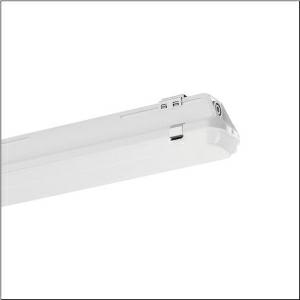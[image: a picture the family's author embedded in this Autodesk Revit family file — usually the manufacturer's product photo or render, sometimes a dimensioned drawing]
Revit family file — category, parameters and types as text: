
# Revit family: monsun_r__12_51fp12mp4b0q_0d1b
name_source: partatom
category: Lighting Fixtures
units: mm (PartAtom-declared; Revit-internal decimal feet)

## family parameters
Cut with Voids When Loaded = No
Host = Face
Light Source = No
Part Type = Normal
Room Calculation Point = No
Round Connector Dimension = Use Diameter
Shared = No

## types (1)
- --- (1 x LED, 11850 lm, 66.2 W, 4000K)
    Apparent Load = 66 VA
    CIE Flux Codes = 62 86 96 97 100
    Color Rendering = 80
    Color Temperature = 4000K
    Default Elevation = 1800 mm
    Description = Monsun® 12, damp-proof luminaire, chain hanger, primary light control with lens, primary optical cover: enclosure, of PMMA, light emission: direct distribution, primary light characteristic: symmetric, installation type: suspended mounting, surface-mounted, horizontal mounting, vertical mounting, LED rated luminous flux: 11.850 lm, light colour: 840, colour temperature: 4000K, control gear: ECG, with terminal, 3-pole, max. 2.5mm², mains connection: 220..240V, AC, 50/60Hz, rated input power: 66W, luminaire housing, of glass-fibre reinforced polyester, uncoated, bright grey, length: 1.590 mm, width: 90 mm, height: 88mm, clip for enclosure, of stainless steel (V2A), ceiling mounting element, of stainless steel (V2A), chain hanger, of stainless steel (V2A), protection rating (complete): IP66, insulation class (complete): insulation class I (protective earthing), certification: CE, ENEC, VDE, protection symbol: D, impact resistance: IK04, permissible ambient temperature for indoor applications: -35..+35°C, standard: EN 50419, EN 60598-2-1, no direct snow, no direct sun, no direct rain, for indoor or canopied outdoor use, corresponds to IFS (International Featured Standards) requirements for safety and quality in the food industry, for animal farming (ammonia tested): for use in cowhouse, pig house, horse-stables... (not for use in poultry stables), AT max for animal farming = 40°C, packaging unit: 1 piece
    Height = 89 mm
    Lamp = 1 x LED
    Lamp Light Flux = 11850 lm
    Lamp Power = 66.2 W
    Lamp count = 1
    Length = 1590 mm
    Luminous efficacy = 179 lm/W
    Manufacturer = Siteco
    ModVariant = No
    Model = 51FP12MP4B0Q
    Mounting Place = Ceiling
    Mounting Type = Pendant
    Number of Poles = 1
    OnlyDefault = Yes
    Power Factor = 1
    Product Name = Monsun® 12
    Product group = damp-proof luminaire | ceiling pendant
    ProductGroupID = 908
    Protection Class = Protection class I
    Protection Degree = IP 66
    RLX_Detail_Level = 1
    RlxData = <blob elided: 89845 chars, md5=4c333159>
    Socket = socket
    Standby Power = 0 W
    System Light Flux = 11850 lm
    System Power = 66 W
    Type Comments = factory setting: luminous flux: 100 % | (A | C | E) | 155 mA
    Type Image = l_1004748.jpg
    URL = http://relux.com
    VarID = @adj_136021
    Voltage = 0 V
    Weight = 0.00 kg
    Width = 90 mm

## geometry (parser evidence)
native form markers: Blend x4, Sweep x11
no freeform markers — native parametric forms only
